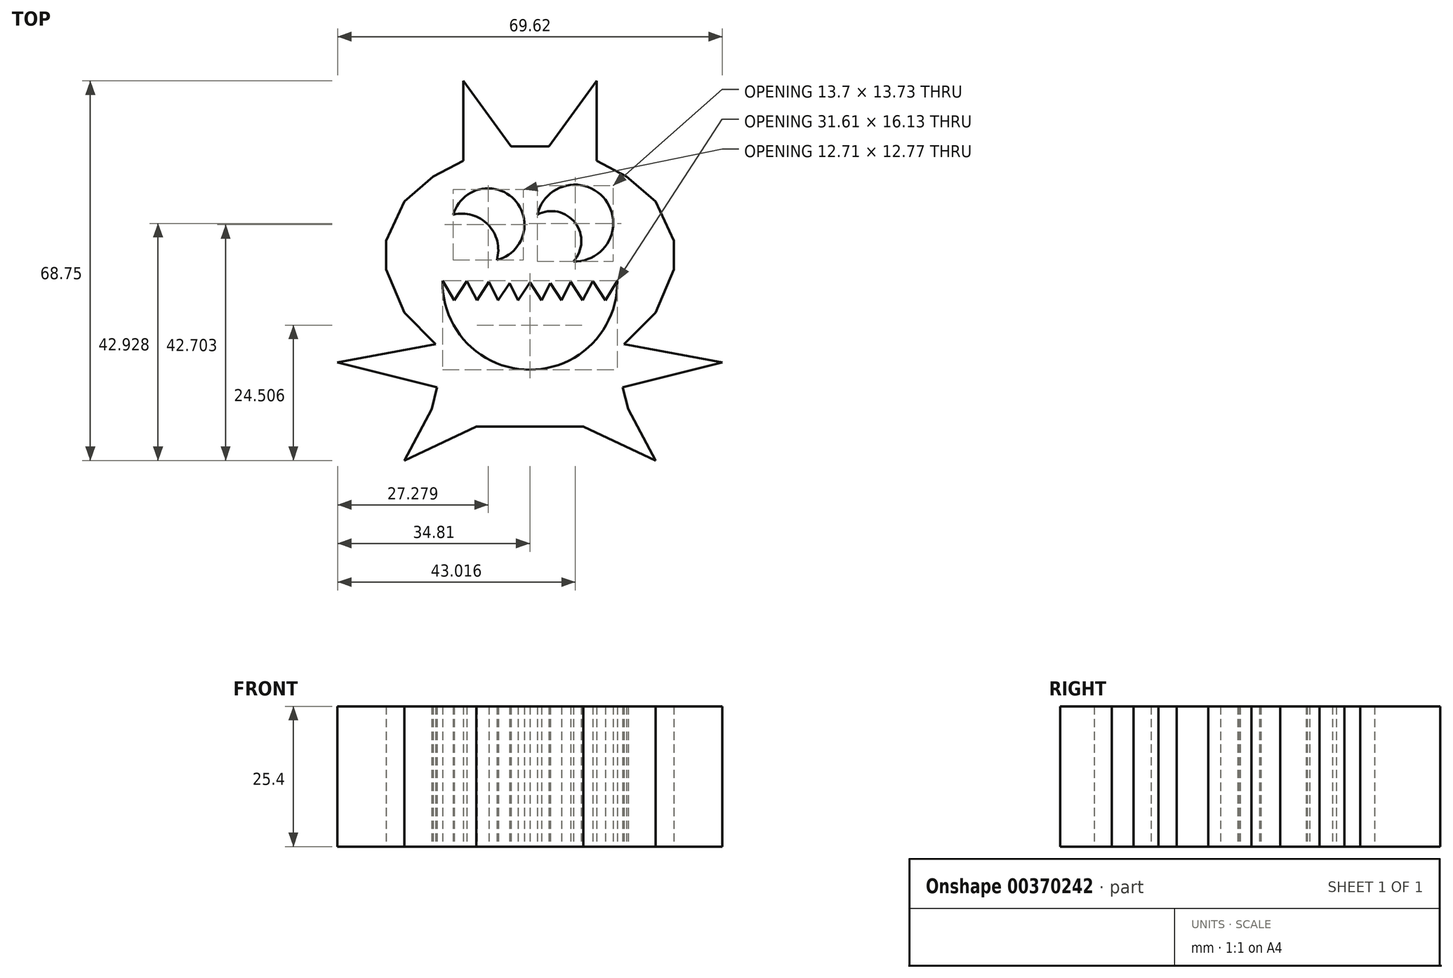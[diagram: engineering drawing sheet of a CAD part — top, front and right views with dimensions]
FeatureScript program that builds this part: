
annotation { "Feature Type Name" : "Feature", "Feature Type Description" : "" }
export const myFeature = defineFeature(function(context is Context, id is Id, definition is map)
    precondition{}
    {
        {
            var Q0;
            Q0=qCreatedBy(makeId("Top.planeOp"),FACE);
            var sketch = newSketch(context, id + "F0", { "sketchPlane" : qUnion([Q0])});
            skLineSegment(sketch, "E0", {"start": v(0, 52.81) * mm, "end": v(3.44, 52.81) * mm});
            skLineSegment(sketch, "E1", {"start": v(3.44, 52.81) * mm, "end": v(12.06, 64.65) * mm});
            skLineSegment(sketch, "E2", {"start": v(12.06, 64.65) * mm, "end": v(12.06, 50.19) * mm});
            skLineSegment(sketch, "E3", {"start": v(12.06, 50.19) * mm, "end": v(17.5, 47.34) * mm});
            skLineSegment(sketch, "E4", {"start": v(17.5, 47.34) * mm, "end": v(22.72, 42.84) * mm});
            skLineSegment(sketch, "E5", {"start": v(22.72, 42.84) * mm, "end": v(26.04, 35.73) * mm});
            skLineSegment(sketch, "E6", {"start": v(26.04, 35.73) * mm, "end": v(26.04, 30.51) * mm});
            skLineSegment(sketch, "E7", {"start": v(26.04, 30.51) * mm, "end": v(22.72, 22.69) * mm});
            skLineSegment(sketch, "E8", {"start": v(22.72, 22.69) * mm, "end": v(17.03, 17) * mm});
            skLineSegment(sketch, "E9", {"start": v(17.03, 17) * mm, "end": v(34.81, 13.68) * mm});
            skLineSegment(sketch, "E10", {"start": v(34.81, 13.68) * mm, "end": v(16.8, 9.17) * mm});
            skLineSegment(sketch, "E11", {"start": v(16.8, 9.17) * mm, "end": v(17.79, 5.21) * mm});
            skLineSegment(sketch, "E12", {"start": v(17.79, 5.21) * mm, "end": v(22.72, -4.1) * mm});
            skLineSegment(sketch, "E13", {"start": v(22.72, -4.1) * mm, "end": v(9.68, 2.06) * mm});
            skLineSegment(sketch, "E14", {"start": v(9.68, 2.06) * mm, "end": v(0, 2.06) * mm});
            skPoint(sketch, "E15.MirrorCS.start.orphan", {"position": v(0, 52.81) * mm});
            skPoint(sketch, "E16.MirrorCS.end.orphan", {"position": v(0, 2.06) * mm});
            skArc(sketch, "E17", {"start": v(7.87, 31.96) * mm, "mid": v(13.64, 43.14) * mm, "end": v(1.36, 40.43) * mm});
            skArc(sketch, "E18", {"start": v(7.87, 31.96) * mm, "mid": v(8.2, 38.95) * mm, "end": v(1.36, 40.43) * mm});
            skLineSegment(sketch, "E19", {"start": v(2.1, 24.9) * mm, "end": v(3.7, 28.05) * mm});
            skLineSegment(sketch, "E20", {"start": v(3.7, 28.05) * mm, "end": v(5.73, 24.9) * mm});
            skLineSegment(sketch, "E21", {"start": v(5.73, 24.9) * mm, "end": v(7.38, 28.28) * mm});
            skLineSegment(sketch, "E22", {"start": v(7.38, 28.28) * mm, "end": v(9.57, 24.9) * mm});
            skLineSegment(sketch, "E23", {"start": v(9.57, 24.9) * mm, "end": v(11.41, 28.4) * mm});
            skLineSegment(sketch, "E24", {"start": v(11.41, 28.4) * mm, "end": v(13.67, 24.9) * mm});
            skPoint(sketch, "E25.start.orphan", {"position": v(0, 28.15) * mm});
            skLineSegment(sketch, "E26", {"start": v(0, 28.15) * mm, "end": v(2.1, 24.9) * mm});
            skLineSegment(sketch, "E27", {"start": v(13.67, 24.9) * mm, "end": v(15.8, 28.47) * mm});
            skLineSegment(sketch, "E28", {"start": v(0, 12.34) * mm, "end": v(0, 12.24) * mm});
            skArc(sketch, "E29", {"start": v(0, 12.34) * mm, "mid": v(11.3, 17.09) * mm, "end": v(15.8, 28.47) * mm});
            skLineSegment(sketch, "E30.MirrorCS", {"start": v(-7.38, 28.28) * mm, "end": v(-9.57, 24.9) * mm});
            skLineSegment(sketch, "E31.MirrorCS", {"start": v(-2.1, 24.9) * mm, "end": v(-3.7, 28.05) * mm});
            skLineSegment(sketch, "E32.MirrorCS", {"start": v(-9.57, 24.9) * mm, "end": v(-11.41, 28.4) * mm});
            skLineSegment(sketch, "E33.MirrorCS", {"start": v(-3.7, 28.05) * mm, "end": v(-5.73, 24.9) * mm});
            skLineSegment(sketch, "E34.MirrorCS", {"start": v(-5.73, 24.9) * mm, "end": v(-7.38, 28.28) * mm});
            skLineSegment(sketch, "E35.MirrorCS", {"start": v(0, 28.15) * mm, "end": v(-2.1, 24.9) * mm});
            skLineSegment(sketch, "E36.MirrorCS", {"start": v(-12.06, 50.19) * mm, "end": v(-17.5, 47.34) * mm});
            skLineSegment(sketch, "E37.MirrorCS", {"start": v(0, 52.81) * mm, "end": v(-3.44, 52.81) * mm});
            skLineSegment(sketch, "E38.MirrorCS", {"start": v(-16.8, 9.17) * mm, "end": v(-17.79, 5.21) * mm});
            skLineSegment(sketch, "E39.MirrorCS", {"start": v(-13.67, 24.9) * mm, "end": v(-15.8, 28.47) * mm});
            skLineSegment(sketch, "E40.MirrorCS", {"start": v(-26.04, 30.51) * mm, "end": v(-22.72, 22.69) * mm});
            skLineSegment(sketch, "E41.MirrorCS", {"start": v(-26.04, 35.73) * mm, "end": v(-26.04, 30.51) * mm});
            skLineSegment(sketch, "E42.MirrorCS", {"start": v(-22.72, 22.69) * mm, "end": v(-17.03, 17) * mm});
            skLineSegment(sketch, "E43.MirrorCS", {"start": v(-17.5, 47.34) * mm, "end": v(-22.72, 42.84) * mm});
            skLineSegment(sketch, "E44.MirrorCS", {"start": v(-22.72, 42.84) * mm, "end": v(-26.04, 35.73) * mm});
            skLineSegment(sketch, "E45.MirrorCS", {"start": v(-11.41, 28.4) * mm, "end": v(-13.67, 24.9) * mm});
            skLineSegment(sketch, "E46.MirrorCS", {"start": v(-3.44, 52.81) * mm, "end": v(-12.06, 64.65) * mm});
            skLineSegment(sketch, "E47.MirrorCS", {"start": v(-17.79, 5.21) * mm, "end": v(-22.72, -4.1) * mm});
            skLineSegment(sketch, "E48.MirrorCS", {"start": v(-12.06, 64.65) * mm, "end": v(-12.06, 50.19) * mm});
            skArc(sketch, "E49.MirrorCS", {"start": v(0, 12.34) * mm, "mid": v(-11.3, 17.09) * mm, "end": v(-15.8, 28.47) * mm});
            skLineSegment(sketch, "E50.MirrorCS", {"start": v(-17.03, 17) * mm, "end": v(-34.81, 13.68) * mm});
            skLineSegment(sketch, "E51.MirrorCS", {"start": v(-34.81, 13.68) * mm, "end": v(-16.8, 9.17) * mm});
            skLineSegment(sketch, "E52.MirrorCS", {"start": v(-9.68, 2.06) * mm, "end": v(0, 2.06) * mm});
            skLineSegment(sketch, "E53.MirrorCS", {"start": v(-22.72, -4.1) * mm, "end": v(-9.68, 2.06) * mm});
            skPoint(sketch, "E54.MirrorCS.end.orphan", {"position": v(-1.36, 40.43) * mm});
            skArc(sketch, "E55", {"start": v(-5.98, 32.22) * mm, "mid": v(-2.83, 43.18) * mm, "end": v(-13.89, 40.41) * mm});
            skArc(sketch, "E56", {"start": v(-5.98, 32.22) * mm, "mid": v(-7.56, 38.6) * mm, "end": v(-13.89, 40.41) * mm});
            skSolve(sketch);
        }
        {
            var Q0;
            Q0 = qSketchRegion(id + "F0", true);
            extrude(context, id + "F1", {"entities" : qUnion([Q0]), "depth" : 25.4 * mm});
        }
    });
